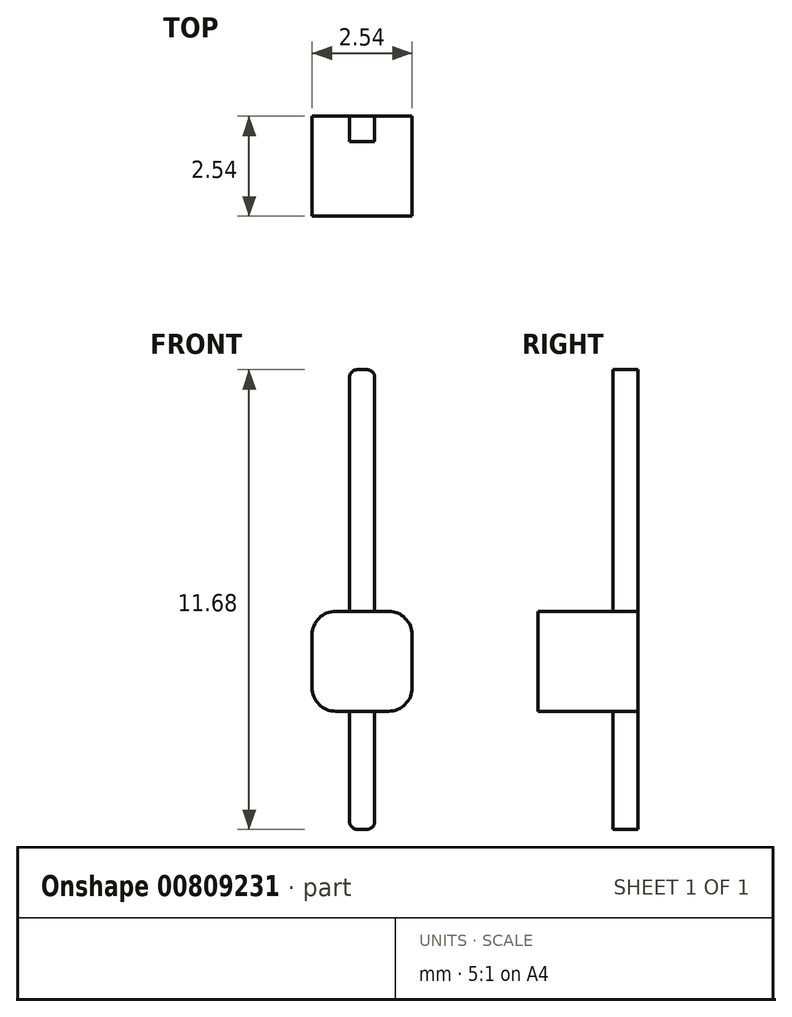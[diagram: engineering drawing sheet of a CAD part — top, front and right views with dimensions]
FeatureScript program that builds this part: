
annotation { "Feature Type Name" : "Feature", "Feature Type Description" : "" }
export const myFeature = defineFeature(function(context is Context, id is Id, definition is map)
    precondition{}
    {
        {
            var Q0;
            Q0=qCreatedBy(makeId("Front.planeOp"),FACE);
            var sketch = newSketch(context, id + "F0", { "sketchPlane" : qUnion([Q0])});
            skLineSegment(sketch, "E0.bottom", {"start": v(-0.67, 1.27) * mm, "end": v(0.67, 1.27) * mm});
            skLineSegment(sketch, "E0.top", {"start": v(-0.67, -1.27) * mm, "end": v(0.67, -1.27) * mm});
            skLineSegment(sketch, "E0.left", {"start": v(-1.27, 0.67) * mm, "end": v(-1.27, -0.67) * mm});
            skLineSegment(sketch, "E0.right", {"start": v(1.27, 0.67) * mm, "end": v(1.27, -0.67) * mm});
            skPoint(sketch, "E1.startSnap0", {"position": v(-1.27, 0) * mm});
            skLineSegment(sketch, "E2", {"start": v(0, -1.27) * mm, "end": v(0, 0) * mm, "construction": true});
            skLineSegment(sketch, "E3", {"start": v(0, 0) * mm, "end": v(-1.27, 0) * mm, "construction": true});
            skLineSegment(sketch, "E4.bottom", {"start": v(-0.12, 7.4) * mm, "end": v(0.12, 7.4) * mm});
            skLineSegment(sketch, "E4.top", {"start": v(-0.12, -4.27) * mm, "end": v(0.12, -4.27) * mm});
            skLineSegment(sketch, "E4.left", {"start": v(-0.32, 7.2) * mm, "end": v(-0.32, -4.07) * mm});
            skLineSegment(sketch, "E4.right", {"start": v(0.32, 7.2) * mm, "end": v(0.32, -4.07) * mm});
            skLineSegment(sketch, "E5", {"start": v(0, -4.27) * mm, "end": v(0, -1.27) * mm, "construction": true});
            skPoint(sketch, "E6.visualSharp", {"position": v(1.27, 1.27) * mm});
            skArc(sketch, "E6.filletArc", {"start": v(1.27, 0.67) * mm, "mid": v(1.1, 1.1) * mm, "end": v(0.67, 1.27) * mm});
            skPoint(sketch, "E7.visualSharp", {"position": v(1.27, -1.27) * mm});
            skArc(sketch, "E7.filletArc", {"start": v(0.67, -1.27) * mm, "mid": v(1.1, -1.1) * mm, "end": v(1.27, -0.67) * mm});
            skPoint(sketch, "E8.visualSharp", {"position": v(-1.27, -1.27) * mm});
            skArc(sketch, "E8.filletArc", {"start": v(-1.27, -0.67) * mm, "mid": v(-1.1, -1.1) * mm, "end": v(-0.67, -1.27) * mm});
            skPoint(sketch, "E9.visualSharp", {"position": v(-1.27, 1.27) * mm});
            skArc(sketch, "E9.filletArc", {"start": v(-0.67, 1.27) * mm, "mid": v(-1.1, 1.1) * mm, "end": v(-1.27, 0.67) * mm});
            skPoint(sketch, "E10.visualSharp", {"position": v(0.32, -4.27) * mm});
            skArc(sketch, "E10.filletArc", {"start": v(0.12, -4.27) * mm, "mid": v(0.26, -4.21) * mm, "end": v(0.32, -4.07) * mm});
            skPoint(sketch, "E11.visualSharp", {"position": v(-0.32, -4.27) * mm});
            skArc(sketch, "E11.filletArc", {"start": v(-0.32, -4.07) * mm, "mid": v(-0.26, -4.21) * mm, "end": v(-0.12, -4.27) * mm});
            skPoint(sketch, "E12.visualSharp", {"position": v(0.32, 7.4) * mm});
            skArc(sketch, "E12.filletArc", {"start": v(0.32, 7.2) * mm, "mid": v(0.26, 7.35) * mm, "end": v(0.12, 7.4) * mm});
            skPoint(sketch, "E13.visualSharp", {"position": v(-0.32, 7.4) * mm});
            skArc(sketch, "E13.filletArc", {"start": v(-0.12, 7.4) * mm, "mid": v(-0.26, 7.35) * mm, "end": v(-0.32, 7.2) * mm});
            skSolve(sketch);
        }
        {
            var Q0;
            Q0=makeQuery(id+"F0.imprint","IMPRINT",FACE,{"disambiguationData":[TD([[makeQuery(id+"F0.imprint","IMPRINT",EDGE,{"derivedFrom":sQuery(id+"F0.wireOp",EDGE,"E0.left")}),1.0]])]});
            var Q1;
            Q1=makeQuery(id+"F0.imprint","IMPRINT",FACE,{"disambiguationData":[TD([[makeQuery(id+"F0.imprint","IMPRINT",EDGE,{"derivedFrom":sQuery(id+"F0.wireOp",EDGE,"E0.right")}),-1.0]])]});
            var Q2;
            {var subQ0=sQuery(id+"F0.wireOp",EDGE,"E4.left");var subQ1=sQuery(id+"F0.wireOp",EDGE,"E0.bottom");var subQ2=makeQuery(id+"F0.imprint","INTERSECT",VERTEX,{"derivedFrom":[subQ1,subQ0]});Q2=makeQuery(id+"F0.imprint","IMPRINT",FACE,{"disambiguationData":[TD([[makeQuery(id+"F0.imprint","IMPRINT",EDGE,{"disambiguationData":[TD([[subQ2,-1.0]])],"derivedFrom":subQ1}),-1.0]])]});}
            extrude(context, id + "F1", {"entities" : qUnion([Q0, Q1, Q2]), "depth" : 2.54 * mm, "offsetDistance" : 25 * mm});
        }
        {
            var Q0;
            Q0=makeQuery(id+"F0.imprint","IMPRINT",FACE,{"disambiguationData":[TD([[makeQuery(id+"F0.imprint","IMPRINT",EDGE,{"derivedFrom":sQuery(id+"F0.wireOp",EDGE,"E4.bottom")}),-1.0]])]});
            var Q1;
            {var subQ0=sQuery(id+"F0.wireOp",EDGE,"E4.left");var subQ1=sQuery(id+"F0.wireOp",EDGE,"E0.bottom");var subQ2=makeQuery(id+"F0.imprint","INTERSECT",VERTEX,{"derivedFrom":[subQ1,subQ0]});Q1=makeQuery(id+"F0.imprint","IMPRINT",FACE,{"disambiguationData":[TD([[makeQuery(id+"F0.imprint","IMPRINT",EDGE,{"disambiguationData":[TD([[subQ2,-1.0]])],"derivedFrom":subQ1}),-1.0]])]});}
            var Q2;
            Q2 = qSketchRegion(id + "F0", true);
            extrude(context, id + "F2", {"entities" : qUnion([Q0, Q1, Q2]), "operationType" : NewBodyOperationType.ADD, "depth" : 0.64 * mm, "offsetDistance" : 25 * mm});
        }
    });
